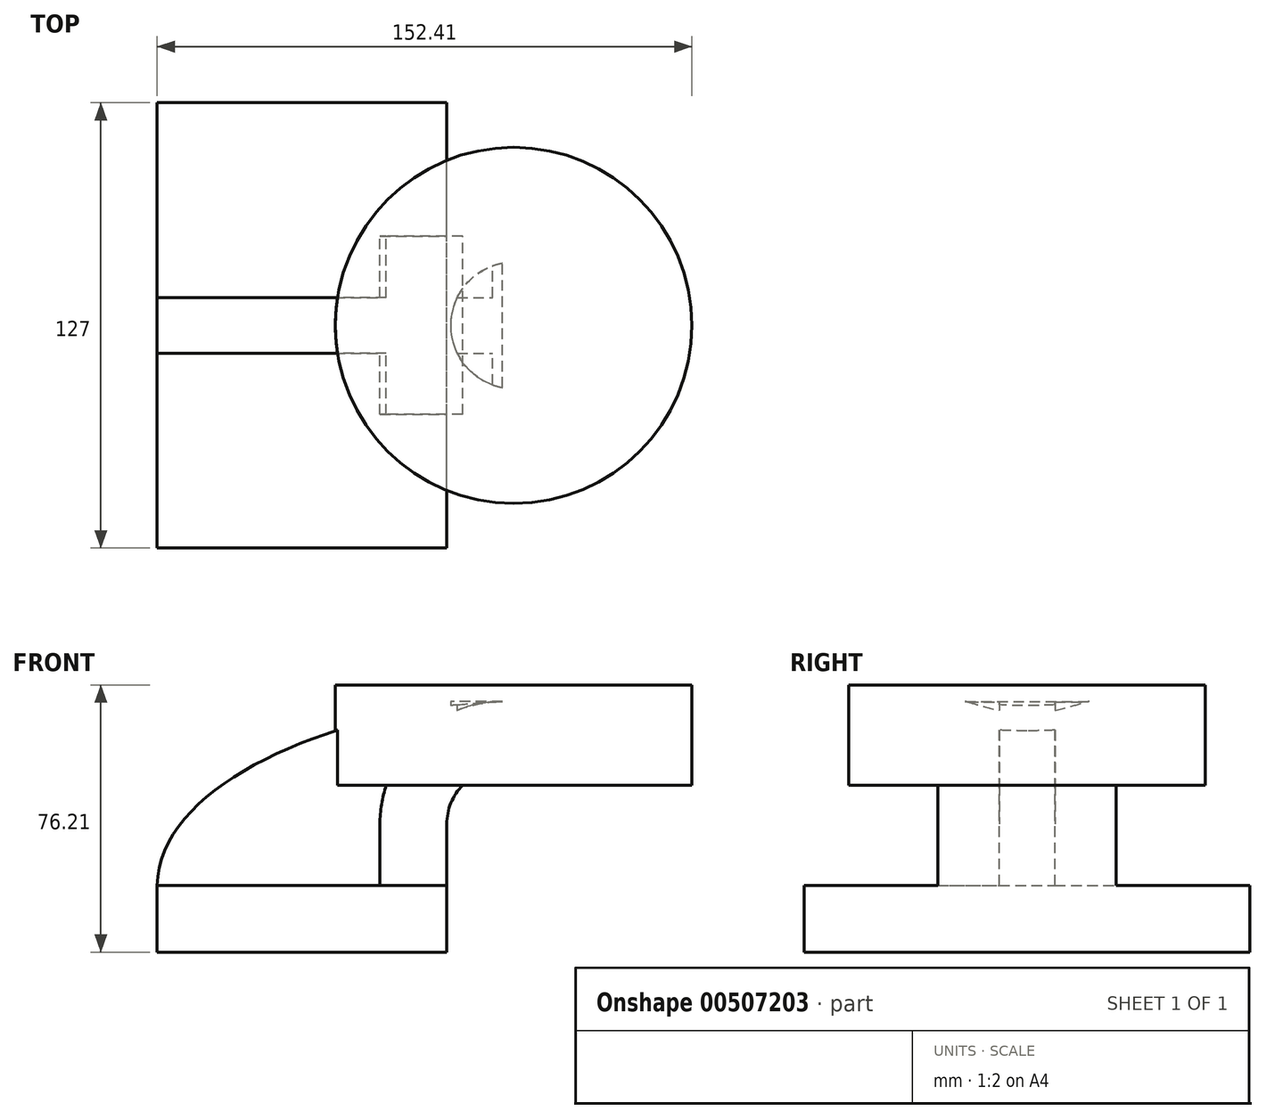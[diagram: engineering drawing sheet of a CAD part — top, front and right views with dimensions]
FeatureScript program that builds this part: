
annotation { "Feature Type Name" : "Feature", "Feature Type Description" : "" }
export const myFeature = defineFeature(function(context is Context, id is Id, definition is map)
    precondition{}
    {
        {
            var Q0;
            Q0=qCreatedBy(makeId("Front.planeOp"),FACE);
            var sketch = newSketch(context, id + "F0", { "sketchPlane" : qUnion([Q0])});
            skLineSegment(sketch, "E0.bottom", {"start": v(-41.28, 9.52) * mm, "end": v(41.27, 9.53) * mm});
            skLineSegment(sketch, "E0.top", {"start": v(-41.28, -9.52) * mm, "end": v(41.28, -9.52) * mm});
            skLineSegment(sketch, "E0.left", {"start": v(-41.28, 9.52) * mm, "end": v(-41.28, -9.53) * mm});
            skLineSegment(sketch, "E0.right", {"start": v(41.27, 9.53) * mm, "end": v(41.28, -9.52) * mm});
            skPoint(sketch, "E0.middle", {"position": v(0, 0) * mm});
            skLineSegment(sketch, "E1.bottom", {"start": v(111.12, 38.1) * mm, "end": v(60.32, 38.1) * mm});
            skLineSegment(sketch, "E1.top", {"start": v(111.12, 66.68) * mm, "end": v(60.32, 66.68) * mm});
            skLineSegment(sketch, "E1.left", {"start": v(111.12, 38.1) * mm, "end": v(111.12, 66.68) * mm});
            skLineSegment(sketch, "E1.right", {"start": v(60.32, 38.1) * mm, "end": v(60.32, 66.68) * mm});
            skPoint(sketch, "E1.middle", {"position": v(85.72, 52.39) * mm});
            skLineSegment(sketch, "E2", {"start": v(41.27, 9.53) * mm, "end": v(41.27, 27) * mm});
            skArc(sketch, "E3", {"start": v(41.27, 27) * mm, "mid": v(45.92, 38.23) * mm, "end": v(57.15, 42.88) * mm});
            skLineSegment(sketch, "E4", {"start": v(57.15, 42.88) * mm, "end": v(78.3, 42.88) * mm});
            skLineSegment(sketch, "E5.0", {"start": v(57.15, 61.93) * mm, "end": v(78.3, 61.93) * mm});
            skArc(sketch, "E5.1", {"start": v(22.22, 27) * mm, "mid": v(32.45, 51.7) * mm, "end": v(57.15, 61.93) * mm});
            skLineSegment(sketch, "E5.2", {"start": v(22.22, 9.53) * mm, "end": v(22.22, 27) * mm});
            skLineSegment(sketch, "E6", {"start": v(78.3, 42.88) * mm, "end": v(78.3, 61.93) * mm});
            skFitSpline(sketch, "E7", {"points": [v(-41.28, 9.52) * mm, v(57.15, 61.93) * mm], "startDerivative": vector(1.5, 90.7) * mm, "endDerivative": vector(131.37, 4.2) * mm});
            skSolve(sketch);
        }
        {
            var Q0;
            Q0=makeQuery(id+"F0.imprint","IMPRINT",FACE,{"disambiguationData":[TD([[makeQuery(id+"F0.imprint","IMPRINT",EDGE,{"derivedFrom":sQuery(id+"F0.wireOp",EDGE,"E0.top")}),1.0]])]});
            extrude(context, id + "F1", {"entities" : qUnion([Q0]), "endBound" : BoundingType.SYMMETRIC, "depth" : 127 * mm});
        }
        {
            var Q0;
            {var subQ1=sQuery(id+"F0.wireOp",EDGE,"E2");Q0=makeQuery(id+"F0.imprint","IMPRINT",FACE,{"disambiguationData":[TD([[makeQuery(id+"F0.imprint","IMPRINT",EDGE,{"derivedFrom":subQ1}),1.0]])]});}
            var Q1;
            {var subQ5=sQuery(id+"F0.wireOp",EDGE,"E6");Q1=makeQuery(id+"F0.imprint","IMPRINT",FACE,{"disambiguationData":[TD([[makeQuery(id+"F0.imprint","IMPRINT",EDGE,{"derivedFrom":subQ5}),1.0]])]});}
            extrude(context, id + "F2", {"entities" : qUnion([Q0, Q1]), "operationType" : NewBodyOperationType.ADD, "endBound" : BoundingType.SYMMETRIC, "depth" : 50.8 * mm});
        }
        {
            var Q0;
            {var subQ3=sQuery(id+"F0.wireOp",EDGE,"E5.2");Q0=makeQuery(id+"F0.imprint","IMPRINT",FACE,{"disambiguationData":[TD([[makeQuery(id+"F0.imprint","IMPRINT",EDGE,{"derivedFrom":subQ3}),1.0]])]});}
            extrude(context, id + "F3", {"entities" : qUnion([Q0]), "operationType" : NewBodyOperationType.ADD, "endBound" : BoundingType.SYMMETRIC, "depth" : 15.88 * mm});
        }
        {
            var Q0;
            {var subQ1=sQuery(id+"F0.wireOp",EDGE,"E1.bottom");Q0=makeQuery(id+"F0.imprint","IMPRINT",FACE,{"disambiguationData":[TD([[makeQuery(id+"F0.imprint","IMPRINT",EDGE,{"derivedFrom":subQ1}),-1.0]])]});}
            var Q1;
            Q1=sQuery(id+"F0.wireOp",EDGE,"E1.right");
            revolve(context, id + "F4", {"operationType" : NewBodyOperationType.ADD, "entities" : qUnion([Q0]), "axis" : qUnion([Q1]), "revolveType" : RevolveType.FULL});
        }
    });
